# Revit family: IS_Tip_K8134_BIM_NL
name_source: partatom
category: Plumbing Fixtures
revit_build: Autodesk Revit MEP 2014 (Build: 20130308_1515(x64)
units: mm (PartAtom-declared; Revit-internal decimal feet)

## types (1)
- K813401 - DUOBAD 180 X 80 CM VOOR INBOUWMONTAGE
    Accessories = www.idealstandardnederland.nl
    AreaUnits = millimeters
    Assembly Code = C1030200
    AssetType = Vast
    BIMObjectName = ISI_IdealStandard_Baths_K813401
    BREEAM = No
    BarCode = 4015413056014
    BathType = Domestic
    Brand = Ideal Standard
    Category = SanitaryTerminal_BATH_UK
    CodePerformance = DIN EN 14516, DIN EN 232, DIN EN 198
    Color = Wit
    ConnectionType = Sanitair
    Cost = 0 $
    Default Elevation = 610 mm  [stored 2.00131 ft]
    Description = Hotline duobad 1800 x 800 mm van acryl. Vervaardigd volgens EN 198. Met glasvezel verstevigd. Ingewerkte bodem- en randversteviging. Afvoergat Ø52 mm. 2 rugleuningen. Potenset separaat te bestellen.
    DrainSize = 38 mm
    DurationUnit = jaar
    ECA = No
    ExpectedLife = 25
    Features = Duobad 1800 x 800 mm van acryl. Vervaardigd volgens EN 198. Met glasvezel verstevigd. Ingewerkte bodem- en randversteviging. Afvoergat Ø52 mm. 2 rugleuningen. Potenset separaat te bestellen.
    Finish = Wit
    HWFU = 0
    HasGrabHandles = No
    IfcExportAs = IfcSanitaryTerminalType
    IfcExportType = BATH
    InstallationInstructions = http://www.idealstandardnederland.nl
    LinearUnits = millimeters
    ManufacturerURL = www.idealstandardnederland.nl
    Material = Acryl
    MaterialThickness = 0 mm  [stored 0 ft]
    Model = K813401
    ModelNumber = K813401
    ModelReference = Hotline duobad 1800 x 800 mm van acryl. Vervaardigd volgens EN 198. Met glasvezel verstevigd. Ingewerkte bodem- en randversteviging. Afvoergat Ø52 mm. 2 rugleuningen. Potenset separaat te bestellen.
    NBSDescription = Baths
    NBSReference = 45-35-70/311
    Name = Baths_K813401_IdealStandard
    NettWeight = 24 kg
    NominalDepth = 800 mm
    NominalHeight = 443 mm
    NominalLength = 800 mm
    NominalWidth = 1800 mm
    ProductInformation = http://www.idealstandardnederland.nl
    Shape = Rechthoekig
    Size = 1800 x 800 x 443 mm
    Space = Internal
    SpareParts = www.idealstandardnederland.nl
    TMV3 = No
    URL = www.idealstandardnederland.nl
    Uniclass2015Code = Pr_40_20_06_08
    Uniclass2015Title = Baths
    Uniclass2015Version = Products v1.1
    Version = 1
    VolumeUnits = liter
    WRAS = No
    WarrantyDescription = Fabrieksgarantie
    WarrantyDurationParts = 5
    WarrantyDurationUnit = jaar
    WaterEfficientProduct = No

note: [stored X ft] marks values corroborated as IEEE doubles in the binary element streams (Revit-internal decimal feet)

## geometry (parser evidence)
native form markers: Sweep x1
no freeform markers — native parametric forms only
